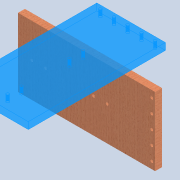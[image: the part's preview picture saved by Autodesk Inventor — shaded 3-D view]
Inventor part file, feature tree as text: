
AUTODESK INVENTOR PART (.ipt)
format: ipt  version: 2020 (Build 240168000, 168)  size: 145,408 bytes
history: native  units: mm
features: sketch x3, hole x2, pattern_linear x2, extrude x1
ambient origin geometry x8: Origin, YZ Plane, XZ Plane, XY Plane, X Axis, Y Axis, Z Axis, Center Point
bodies: Solid1 (feature_tree)
feature tree (8):
  extrude  "Extrusion1"  Depth=200.0mm
  hole  "Hole1"  [1 undecoded]
  pattern_linear  "Rectangular Pattern1"  Count1=2  [1 undecoded]
  hole  "Hole2"  [1 undecoded]
  pattern_linear  "Rectangular Pattern2"  Count1=5  [1 undecoded]
  sketch  "Sketch1"  dims[d0=400.0mm d1=200.0mm]
  sketch  "Sketch10"  dims[d2=20.0mm d3=0.0mm]
  sketch  "Sketch11"  dims[d46=8.0mm d47=6.0mm d48=4.0mm d49=2.0mm d50=90.0deg d51=8.0mm d52=20.594885mm d53=40.0mm d54=20.0mm d56=40.0mm d57=10.0mm d58=8.0mm d59=6.0mm d60=4.0mm d61=2.0mm d62=90.0deg d63=8.0mm d64=20.594885mm d65=50.0mm d67=40.0mm d68=20.0mm d70=180.0mm]
note: 4 required parameter values undecoded (feature->parameter linkage not recoverable at this tier; creation-order binding heuristic only, values carry confidence <= 0.55)
